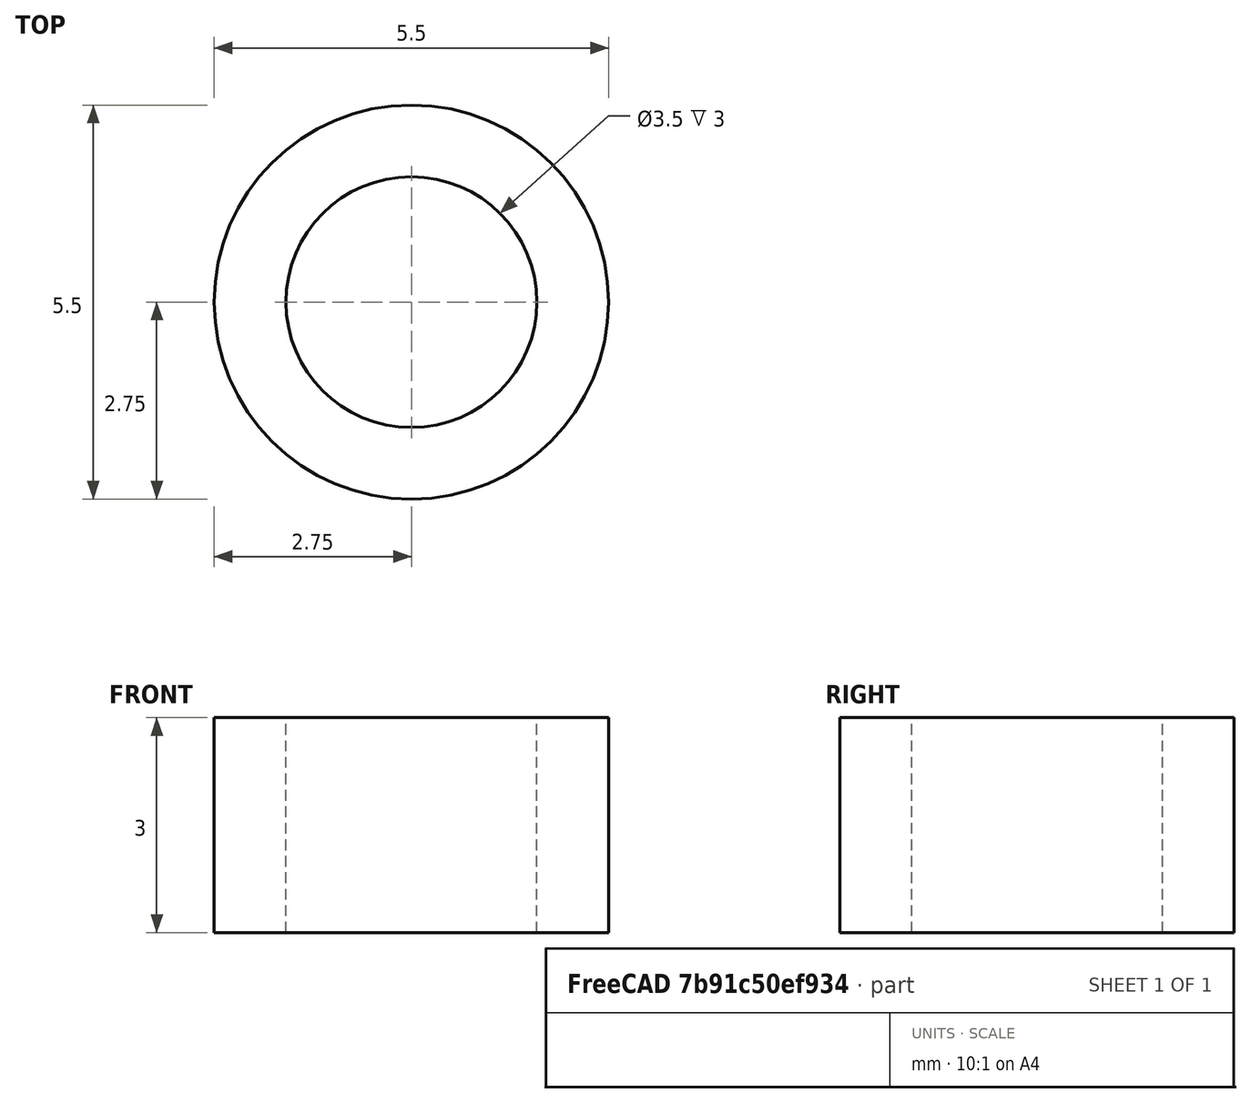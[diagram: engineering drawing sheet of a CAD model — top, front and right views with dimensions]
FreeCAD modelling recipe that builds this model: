
FCSTD DOCUMENT  (FreeCAD 0.18R16131 (Git))
Label: spacer
License: All rights reserved
LicenseURL: http://en.wikipedia.org/wiki/All_rights_reserved
objects: Part::Cylinder×2, Part::Cut×1, Spreadsheet::Sheet×1
note: 3 computed .brp shape members not serialized (recipe doc carries the construction recipe); baked Part::Feature solids carry a one-line shape summary decoded from their .brp

FEATURE [Part::Cylinder] Cylinder  label="exterior"
  Angle = 360
  AttacherType = Attacher::AttachEngine3D
  Height = 3
  Radius = 2.75
  expr: Height = Spreadsheet.C2
  expr: Radius = Spreadsheet.A2 / 2
FEATURE [Part::Cylinder] Cylinder001  label="interior"
  Angle = 360
  AttacherType = Attacher::AttachEngine3D
  Height = 3
  Radius = 1.75
  expr: Radius = Spreadsheet.B2 / 2
  expr: Height = exterior.Height
FEATURE [Part::Cut] Cut  label="spacer"
  Base = -> Cylinder
  Tool = -> Cylinder001
FEATURE [Spreadsheet::Sheet] Spreadsheet
  cells = A1=ext diameter; B1=int diameter; C1=height; A2=5.5; B2=3.5; C2=3
